# Revit family: Ленточный двухскатный зенитный фонарь M8CITY_Д_ВЕНТ-ДЫМ_1_ств_30_град
name_source: partatom
category: Окна
units: mm (PartAtom-declared; Revit-internal decimal feet)

## family parameters
Всегда вертикально = Нет
Общий = Нет
Основа = Крыша
При загрузке вырезать с полостями = Нет
Точка расчета площади = Нет

## types (1)
- Ленточный двухскатный зенитный фонарь M8CITY_Д_ВЕНТ-ДЫМ_1_ств_30_град
    230В двойной = Нет
    URL = www.m8city.by
    Бренд = M8CITY
    Вид створки = 1
    Видимость привода двойного = Нет
    Видимость створки = Да
    Видимость створки двойной = Нет
    Высота = 573 мм
    Высота основания = 500 мм
    Длина = 4200 мм
    Длина проема = 4200 мм
    Длина проема ввод = 4200 мм
    Длина створки = 3000 мм
    Длина створки ном = 2424.9 мм
    Изготовитель = ООО М8 Сити Про
    Количество арок = 2
    Материал заполнения = <По категории>
    Описание = Ленточный зенитный фонарь M8CITY в премиальном исполнении ВЕНТ/ДЫМ двухскатный
    Отметка по умолчанию = 0 мм
    Привод двойной створки = 0
    Телефон = +375 17 311 09 02, +7 495 946 99 02, +380 50 120 51 80
    Типовой растр = 1060 мм
    Угол = 0.866025
    Шаг типовой = 1060 мм
    Ширина = 4200 мм
    Ширина проема = 4200 мм
    Ширина проема ввод = 4200 мм
